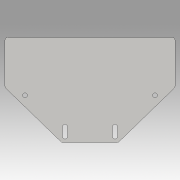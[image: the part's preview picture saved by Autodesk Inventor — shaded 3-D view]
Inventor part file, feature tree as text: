
AUTODESK INVENTOR PART (.ipt)
format: ipt  version: 2016 (Build 200138000, 138)  size: 165,376 bytes
history: native  units: in
note: dims shown in document units (in); Inventor stores cm internally (conversion verified against a paired STEP export)
features: sketch x4, extrude x3, hole x1, fillet x1
ambient origin geometry x8: Origin, YZ Plane, XZ Plane, XY Plane, X Axis, Y Axis, Z Axis, Center Point
bodies: Solid1 (feature_tree)
feature tree (9):
  extrude  "Extrusion1"  Depth=6.0in
  hole  "Hole1"  [1 undecoded]
  sketch  "Sketch3"  dims[d7=3.25in d9=2.0625in]
  sketch  "Sketch4"  dims[d10=0.2953in d11=0.25in d12=0.75in d13=0.375in d14=0.25in d15=0.5635in d16=1.0in d17=0.8108in d20=0.75in d29=0.25in d30=0.5in d32=3.4055in d33=0.0in d34=3.4055in d35=0.3in d36=0.9337in d37=0.9337in d38=0.3in d41=1.4105in d42=1.0in d43=0.0in d44=90.0deg d45=90.0deg d46=90.0deg d48=0.5in d49=0.5in d50=0.5in d53=1.0in d54=0.0in d55=0.125in]
  extrude  "Extrusion3"  Depth=2.0625in
  extrude  "Extrusion5"  Depth=0.125in
  fillet  "Fillet1"  Radius=0.25in
  sketch  "Sketch1"  dims[d0=8.5in d1=6.0in]
  sketch  "Sketch2"  dims[d2=0.125in d3=0.0in d5=1.25in]
note: 1 required parameter value undecoded (feature->parameter linkage not recoverable at this tier; creation-order binding heuristic only, values carry confidence <= 0.55)
